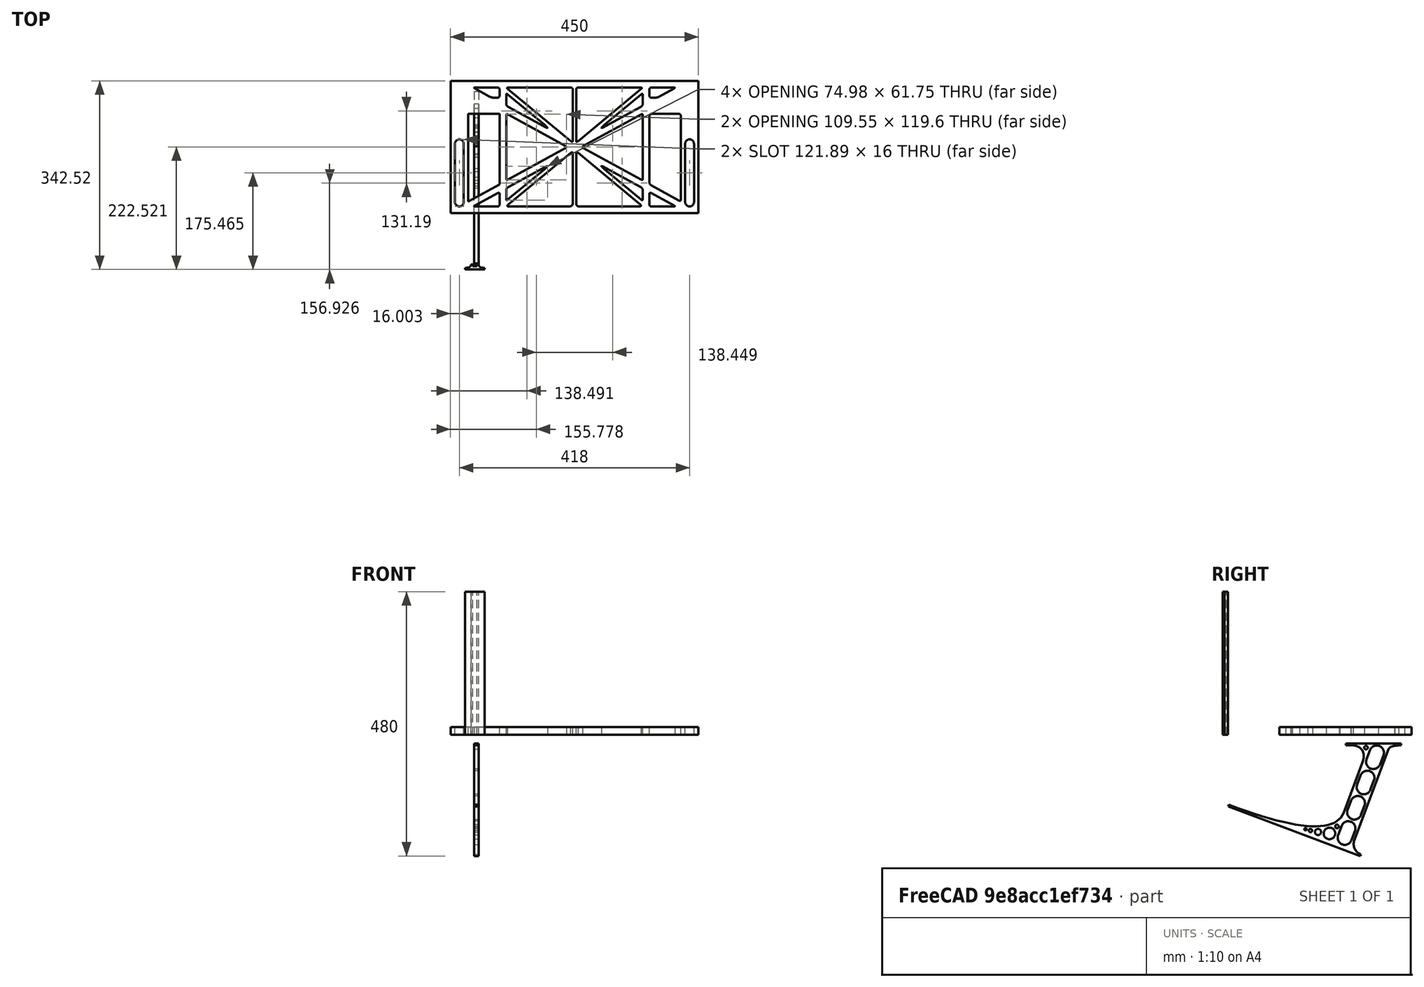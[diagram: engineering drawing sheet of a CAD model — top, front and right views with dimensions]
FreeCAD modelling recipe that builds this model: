
FCSTD DOCUMENT  (FreeCAD 0.19R0.19.2)
Label: laptopStand135FCStd
License: All rights reserved
LicenseURL: http://en.wikipedia.org/wiki/All_rights_reserved
objects: Sketcher::SketchObject×3, Part::Extrusion×3
note: 6 computed .brp shape members not serialized (recipe doc carries the construction recipe); baked Part::Feature solids carry a one-line shape summary decoded from their .brp

FEATURE [Sketcher::SketchObject] Sketch
  FullyConstrained = false
  sketch-geometry (352):
    g0: LineSegment StartX=-10.9272 StartY=-82.7794 StartZ=0 EndX=46.0728 EndY=-51.4823 EndZ=0
    g1: LineSegment StartX=-10.9272 StartY=76.4095 StartZ=0 EndX=-10.9272 EndY=-82.7794 EndZ=0
    g2: LineSegment StartX=46.0728 StartY=76.4095 StartZ=0 EndX=46.0728 EndY=-51.4823 EndZ=0
    g3: LineSegment StartX=-42.9272 StartY=136.221 StartZ=0 EndX=-42.9272 EndY=-103.779 EndZ=0
    g4: LineSegment StartX=407.073 StartY=136.221 StartZ=0 EndX=407.073 EndY=-103.779 EndZ=0
    g5: ArcOfCircle CenterX=-26.9272 CenterY=22.1087 CenterZ=0 NormalX=0 NormalY=0 NormalZ=1 AngleXU=0 Radius=8 StartAngle=4.1e-15 EndAngle=3.14159
    g6: ArcOfCircle CenterX=-26.9272 CenterY=-83.7794 CenterZ=0 NormalX=0 NormalY=0 NormalZ=1 AngleXU=0 Radius=8 StartAngle=3.14159 EndAngle=6.28319
    g7: LineSegment StartX=-34.9272 StartY=22.1087 StartZ=0 EndX=-34.9272 EndY=-83.7794 EndZ=0
    g8: LineSegment StartX=-18.9272 StartY=22.1087 StartZ=0 EndX=-18.9272 EndY=-83.7794 EndZ=0
    g9: ArcOfCircle CenterX=391.073 CenterY=22.1087 CenterZ=0 NormalX=0 NormalY=0 NormalZ=1 AngleXU=0 Radius=8 StartAngle=-4.4e-15 EndAngle=3.14159
    g10: LineSegment StartX=399.073 StartY=22.1087 StartZ=0 EndX=399.073 EndY=-83.7794 EndZ=0
    g11: LineSegment StartX=383.073 StartY=22.1087 StartZ=0 EndX=383.073 EndY=-83.7794 EndZ=0
    g12: ArcOfCircle CenterX=391.073 CenterY=-83.7794 CenterZ=0 NormalX=0 NormalY=0 NormalZ=1 AngleXU=0 Radius=8 StartAngle=3.14159 EndAngle=6.28319
    g13: Circle CenterX=175.022 CenterY=27.0628 CenterZ=0 NormalX=0 NormalY=0 NormalZ=1 AngleXU=0 Radius=1
    g14: Circle CenterX=179.022 CenterY=24.8665 CenterZ=0 NormalX=0 NormalY=0 NormalZ=1 AngleXU=0 Radius=1
    g15: Circle CenterX=179.022 CenterY=27.0628 CenterZ=0 NormalX=0 NormalY=0 NormalZ=1 AngleXU=0 Radius=1
    g16: BSplineCurve PolesCount=3 KnotsCount=2 Degree=2 IsPeriodic=0
    g17: GeomPoint X=175.022 Y=27.0628 Z=0
    g18: GeomPoint X=179.022 Y=27.0628 Z=0
    g19: Circle CenterX=189.124 CenterY=27.0628 CenterZ=0 NormalX=0 NormalY=0 NormalZ=1 AngleXU=0 Radius=1
    g20: Circle CenterX=185.124 CenterY=24.8665 CenterZ=0 NormalX=0 NormalY=0 NormalZ=1 AngleXU=0 Radius=1
    g21: Circle CenterX=185.124 CenterY=27.0628 CenterZ=0 NormalX=0 NormalY=0 NormalZ=1 AngleXU=0 Radius=1
    g22: BSplineCurve PolesCount=3 KnotsCount=2 Degree=2 IsPeriodic=0
    g23: GeomPoint X=189.124 Y=27.0628 Z=0
    g24: GeomPoint X=185.124 Y=27.0628 Z=0
    g25: Circle CenterX=175.022 CenterY=5.37834 CenterZ=0 NormalX=0 NormalY=0 NormalZ=1 AngleXU=0 Radius=1
    g26: Circle CenterX=179.022 CenterY=7.57463 CenterZ=0 NormalX=0 NormalY=0 NormalZ=1 AngleXU=0 Radius=1
    g27: Circle CenterX=179.022 CenterY=5.34704 CenterZ=0 NormalX=0 NormalY=0 NormalZ=1 AngleXU=0 Radius=1
    g28: BSplineCurve PolesCount=3 KnotsCount=2 Degree=2 IsPeriodic=0
    g29: GeomPoint X=175.022 Y=5.37834 Z=0
    g30: GeomPoint X=179.022 Y=5.34704 Z=0
    g31: Circle CenterX=189.124 CenterY=5.37834 CenterZ=0 NormalX=0 NormalY=0 NormalZ=1 AngleXU=0 Radius=1
    g32: Circle CenterX=185.124 CenterY=7.57463 CenterZ=0 NormalX=0 NormalY=0 NormalZ=1 AngleXU=0 Radius=1
    g33: Circle CenterX=185.124 CenterY=5.34704 CenterZ=0 NormalX=0 NormalY=0 NormalZ=1 AngleXU=0 Radius=1
    g34: BSplineCurve PolesCount=3 KnotsCount=2 Degree=2 IsPeriodic=0
    g35: GeomPoint X=189.124 Y=5.37834 Z=0
    g36: GeomPoint X=185.124 Y=5.34704 Z=0
    g37: Circle CenterX=165.871 CenterY=18.1458 CenterZ=0 NormalX=0 NormalY=0 NormalZ=1 AngleXU=0 Radius=1
    g38: Circle CenterX=169.377 CenterY=16.2206 CenterZ=0 NormalX=0 NormalY=0 NormalZ=1 AngleXU=0 Radius=1
    g39: Circle CenterX=165.871 CenterY=14.2954 CenterZ=0 NormalX=0 NormalY=0 NormalZ=1 AngleXU=0 Radius=1
    g40: BSplineCurve PolesCount=3 KnotsCount=2 Degree=2 IsPeriodic=0
    g41: GeomPoint X=165.871 Y=18.1458 Z=0
    g42: GeomPoint X=165.871 Y=14.2954 Z=0
    g43: Circle CenterX=198.275 CenterY=18.1458 CenterZ=0 NormalX=0 NormalY=0 NormalZ=1 AngleXU=0 Radius=1
    g44: Circle CenterX=194.768 CenterY=16.2206 CenterZ=0 NormalX=0 NormalY=0 NormalZ=1 AngleXU=0 Radius=1
    g45: Circle CenterX=198.275 CenterY=14.2954 CenterZ=0 NormalX=0 NormalY=0 NormalZ=1 AngleXU=0 Radius=1
    g46: BSplineCurve PolesCount=3 KnotsCount=2 Degree=2 IsPeriodic=0
    g47: GeomPoint X=198.275 Y=18.1458 Z=0
    g48: GeomPoint X=198.275 Y=14.2954 Z=0
    g49: LineSegment StartX=407.073 StartY=-103.779 StartZ=0 EndX=-42.9272 EndY=-103.779 EndZ=0
    g50: LineSegment StartX=407.073 StartY=136.221 StartZ=0 EndX=-42.9272 EndY=136.221 EndZ=0
    g51: LineSegment StartX=46.0728 StartY=76.4095 StartZ=0 EndX=-10.9272 EndY=76.4095 EndZ=0
    g52: Circle CenterX=125.607 CenterY=54.1951 CenterZ=0 NormalX=0 NormalY=0 NormalZ=1 AngleXU=0 Radius=1
    g53: Circle CenterX=139.632 CenterY=46.4944 CenterZ=0 NormalX=0 NormalY=0 NormalZ=1 AngleXU=0 Radius=1
    g54: Circle CenterX=127.326 CenterY=56.7187 CenterZ=0 NormalX=0 NormalY=0 NormalZ=1 AngleXU=0 Radius=1
    g55: BSplineCurve PolesCount=3 KnotsCount=2 Degree=2 IsPeriodic=0
    g56: GeomPoint X=125.607 Y=54.1951 Z=0
    g57: GeomPoint X=127.326 Y=56.7187 Z=0
    g58: Circle CenterX=236.821 CenterY=56.7187 CenterZ=0 NormalX=0 NormalY=0 NormalZ=1 AngleXU=0 Radius=1
    g59: Circle CenterX=224.513 CenterY=46.4944 CenterZ=0 NormalX=0 NormalY=0 NormalZ=1 AngleXU=0 Radius=1
    g60: Circle CenterX=238.538 CenterY=54.1951 CenterZ=0 NormalX=0 NormalY=0 NormalZ=1 AngleXU=0 Radius=1
    g61: BSplineCurve PolesCount=3 KnotsCount=2 Degree=2 IsPeriodic=0
    g62: GeomPoint X=236.821 Y=56.7187 Z=0
    g63: GeomPoint X=238.538 Y=54.1951 Z=0
    g64: Circle CenterX=238.538 CenterY=-21.7539 CenterZ=0 NormalX=0 NormalY=0 NormalZ=1 AngleXU=0 Radius=1
    g65: Circle CenterX=224.513 CenterY=-14.0532 CenterZ=0 NormalX=0 NormalY=0 NormalZ=1 AngleXU=0 Radius=1
    g66: Circle CenterX=236.821 CenterY=-24.2775 CenterZ=0 NormalX=0 NormalY=0 NormalZ=1 AngleXU=0 Radius=1
    g67: BSplineCurve PolesCount=3 KnotsCount=2 Degree=2 IsPeriodic=0
    g68: GeomPoint X=238.538 Y=-21.7539 Z=0
    g69: GeomPoint X=236.821 Y=-24.2775 Z=0
    g70: Circle CenterX=125.607 CenterY=-21.7539 CenterZ=0 NormalX=0 NormalY=0 NormalZ=1 AngleXU=0 Radius=1
    g71: Circle CenterX=139.632 CenterY=-14.0532 CenterZ=0 NormalX=0 NormalY=0 NormalZ=1 AngleXU=0 Radius=1
    g72: Circle CenterX=127.325 CenterY=-24.2775 CenterZ=0 NormalX=0 NormalY=0 NormalZ=1 AngleXU=0 Radius=1
    g73: BSplineCurve PolesCount=3 KnotsCount=2 Degree=2 IsPeriodic=0
    g74: GeomPoint X=125.607 Y=-21.7539 Z=0
    g75: GeomPoint X=127.325 Y=-24.2775 Z=0
    g76: Circle CenterX=302.996 CenterY=111.695 CenterZ=0 NormalX=0 NormalY=0 NormalZ=1 AngleXU=0 Radius=1
    g77: Circle CenterX=306.073 CenterY=114.251 CenterZ=0 NormalX=0 NormalY=0 NormalZ=1 AngleXU=0 Radius=1
    g78: Circle CenterX=306.073 CenterY=110.251 CenterZ=0 NormalX=0 NormalY=0 NormalZ=1 AngleXU=0 Radius=1
    g79: BSplineCurve PolesCount=3 KnotsCount=2 Degree=2 IsPeriodic=0
    g80: GeomPoint X=302.996 Y=111.695 Z=0
    g81: GeomPoint X=306.073 Y=110.251 Z=0
    g82: Circle CenterX=306.073 CenterY=95.2763 CenterZ=0 NormalX=0 NormalY=0 NormalZ=1 AngleXU=0 Radius=1
    g83: Circle CenterX=306.073 CenterY=91.2763 CenterZ=0 NormalX=0 NormalY=0 NormalZ=1 AngleXU=0 Radius=1
    g84: Circle CenterX=302.567 CenterY=89.3511 CenterZ=0 NormalX=0 NormalY=0 NormalZ=1 AngleXU=0 Radius=1
    g85: BSplineCurve PolesCount=3 KnotsCount=2 Degree=2 IsPeriodic=0
    g86: GeomPoint X=306.073 Y=95.2763 Z=0
    g87: GeomPoint X=302.567 Y=89.3511 Z=0
    g88: LineSegment StartX=306.073 StartY=110.251 StartZ=0 EndX=306.073 EndY=95.2763 EndZ=0
    g89: LineSegment StartX=302.996 StartY=111.695 StartZ=0 EndX=236.821 EndY=56.7187 EndZ=0
    g90: LineSegment StartX=238.538 StartY=54.1951 StartZ=0 EndX=302.567 EndY=89.3511 EndZ=0
    g91: Circle CenterX=61.1496 CenterY=111.695 CenterZ=0 NormalX=0 NormalY=0 NormalZ=1 AngleXU=0 Radius=1
    g92: Circle CenterX=58.0728 CenterY=114.251 CenterZ=0 NormalX=0 NormalY=0 NormalZ=1 AngleXU=0 Radius=1
    g93: Circle CenterX=58.0728 CenterY=110.251 CenterZ=0 NormalX=0 NormalY=0 NormalZ=1 AngleXU=0 Radius=1
    g94: BSplineCurve PolesCount=3 KnotsCount=2 Degree=2 IsPeriodic=0
    g95: GeomPoint X=61.1496 Y=111.695 Z=0
    g96: GeomPoint X=58.0728 Y=110.251 Z=0
    g97: Circle CenterX=61.5791 CenterY=89.3511 CenterZ=0 NormalX=0 NormalY=0 NormalZ=1 AngleXU=0 Radius=1
    g98: Circle CenterX=58.0728 CenterY=91.2763 CenterZ=0 NormalX=0 NormalY=0 NormalZ=1 AngleXU=0 Radius=1
    g99: Circle CenterX=58.0728 CenterY=95.2763 CenterZ=0 NormalX=0 NormalY=0 NormalZ=1 AngleXU=0 Radius=1
    g100: BSplineCurve PolesCount=3 KnotsCount=2 Degree=2 IsPeriodic=0
    g101: GeomPoint X=61.5791 Y=89.3511 Z=0
    g102: GeomPoint X=58.0728 Y=95.2763 Z=0
    g103: LineSegment StartX=58.0728 StartY=110.251 StartZ=0 EndX=58.0728 EndY=95.2763 EndZ=0
    g104: LineSegment StartX=61.1496 StartY=111.695 StartZ=0 EndX=127.326 EndY=56.7187 EndZ=0
    g105: LineSegment StartX=125.607 StartY=54.1951 StartZ=0 EndX=61.5791 EndY=89.3511 EndZ=0
    g106: Circle CenterX=61.5791 CenterY=-56.9099 CenterZ=0 NormalX=0 NormalY=0 NormalZ=1 AngleXU=0 Radius=1
    g107: Circle CenterX=58.0728 CenterY=-58.8351 CenterZ=0 NormalX=0 NormalY=0 NormalZ=1 AngleXU=0 Radius=1
    g108: Circle CenterX=58.0728 CenterY=-62.8351 CenterZ=0 NormalX=0 NormalY=0 NormalZ=1 AngleXU=0 Radius=1
    g109: BSplineCurve PolesCount=3 KnotsCount=2 Degree=2 IsPeriodic=0
    g110: GeomPoint X=61.5791 Y=-56.9099 Z=0
    g111: GeomPoint X=58.0728 Y=-62.8351 Z=0
    g112: Circle CenterX=58.0728 CenterY=-77.8102 CenterZ=0 NormalX=0 NormalY=0 NormalZ=1 AngleXU=0 Radius=1
    g113: Circle CenterX=58.0728 CenterY=-81.8102 CenterZ=0 NormalX=0 NormalY=0 NormalZ=1 AngleXU=0 Radius=1
    g114: Circle CenterX=61.1496 CenterY=-79.2541 CenterZ=0 NormalX=0 NormalY=0 NormalZ=1 AngleXU=0 Radius=1
    g115: BSplineCurve PolesCount=3 KnotsCount=2 Degree=2 IsPeriodic=0
    g116: GeomPoint X=58.0728 Y=-77.8102 Z=0
    g117: GeomPoint X=61.1496 Y=-79.2541 Z=0
    g118: LineSegment StartX=58.0728 StartY=-62.8351 StartZ=0 EndX=58.0728 EndY=-77.8102 EndZ=0
    g119: LineSegment StartX=61.1496 StartY=-79.2541 StartZ=0 EndX=127.325 EndY=-24.2775 EndZ=0
    g120: LineSegment StartX=125.607 StartY=-21.7539 StartZ=0 EndX=61.5791 EndY=-56.9099 EndZ=0
    g121: Circle CenterX=302.567 CenterY=-56.9099 CenterZ=0 NormalX=0 NormalY=0 NormalZ=1 AngleXU=0 Radius=1
    g122: Circle CenterX=306.073 CenterY=-58.8351 CenterZ=0 NormalX=0 NormalY=0 NormalZ=1 AngleXU=0 Radius=1
    g123: Circle CenterX=306.073 CenterY=-62.8351 CenterZ=0 NormalX=0 NormalY=0 NormalZ=1 AngleXU=0 Radius=1
    g124: BSplineCurve PolesCount=3 KnotsCount=2 Degree=2 IsPeriodic=0
    g125: GeomPoint X=302.567 Y=-56.9099 Z=0
    g126: GeomPoint X=306.073 Y=-62.8351 Z=0
    g127: Circle CenterX=302.996 CenterY=-79.2541 CenterZ=0 NormalX=0 NormalY=0 NormalZ=1 AngleXU=0 Radius=1
    g128: Circle CenterX=306.073 CenterY=-81.8102 CenterZ=0 NormalX=0 NormalY=0 NormalZ=1 AngleXU=0 Radius=1
    g129: Circle CenterX=306.073 CenterY=-77.8102 CenterZ=0 NormalX=0 NormalY=0 NormalZ=1 AngleXU=0 Radius=1
    g130: BSplineCurve PolesCount=3 KnotsCount=2 Degree=2 IsPeriodic=0
    g131: GeomPoint X=302.996 Y=-79.2541 Z=0
    g132: GeomPoint X=306.073 Y=-77.8102 Z=0
    g133: LineSegment StartX=306.073 StartY=-62.8351 StartZ=0 EndX=306.073 EndY=-77.8102 EndZ=0
    g134: LineSegment StartX=302.996 StartY=-79.2541 StartZ=0 EndX=236.821 EndY=-24.2775 EndZ=0
    g135: LineSegment StartX=238.538 StartY=-21.7539 StartZ=0 EndX=302.567 EndY=-56.9099 EndZ=0
    g136: Circle CenterX=61.6457 CenterY=-88.8112 CenterZ=0 NormalX=0 NormalY=0 NormalZ=1 AngleXU=0 Radius=1
    g137: Circle CenterX=58.0728 CenterY=-91.7794 CenterZ=0 NormalX=0 NormalY=0 NormalZ=1 AngleXU=0 Radius=1
    g138: Circle CenterX=63.9135 CenterY=-91.7794 CenterZ=0 NormalX=0 NormalY=0 NormalZ=1 AngleXU=0 Radius=1
    g139: BSplineCurve PolesCount=3 KnotsCount=2 Degree=2 IsPeriodic=0
    g140: GeomPoint X=61.6457 Y=-88.8112 Z=0
    g141: GeomPoint X=63.9135 Y=-91.7794 Z=0
    g142: Circle CenterX=179.022 CenterY=-85.8163 CenterZ=0 NormalX=0 NormalY=0 NormalZ=1 AngleXU=0 Radius=1
    g143: Circle CenterX=179.022 CenterY=-91.7794 CenterZ=0 NormalX=0 NormalY=0 NormalZ=1 AngleXU=0 Radius=1
    g144: Circle CenterX=171.895 CenterY=-91.7794 CenterZ=0 NormalX=0 NormalY=0 NormalZ=1 AngleXU=0 Radius=1
    g145: BSplineCurve PolesCount=3 KnotsCount=2 Degree=2 IsPeriodic=0
    g146: GeomPoint X=179.022 Y=-85.8163 Z=0
    g147: GeomPoint X=171.895 Y=-91.7794 Z=0
    g148: Circle CenterX=185.124 CenterY=-86.2028 CenterZ=0 NormalX=0 NormalY=0 NormalZ=1 AngleXU=0 Radius=1
    g149: Circle CenterX=185.124 CenterY=-91.7794 CenterZ=0 NormalX=0 NormalY=0 NormalZ=1 AngleXU=0 Radius=1
    g150: Circle CenterX=191.747 CenterY=-91.7794 CenterZ=0 NormalX=0 NormalY=0 NormalZ=1 AngleXU=0 Radius=1
    g151: BSplineCurve PolesCount=3 KnotsCount=2 Degree=2 IsPeriodic=0
    g152: GeomPoint X=185.124 Y=-86.2028 Z=0
    g153: GeomPoint X=191.747 Y=-91.7794 Z=0
    g154: Circle CenterX=299.888 CenterY=-86.6413 CenterZ=0 NormalX=0 NormalY=0 NormalZ=1 AngleXU=0 Radius=1
    g155: Circle CenterX=306.073 CenterY=-91.7794 CenterZ=0 NormalX=0 NormalY=0 NormalZ=1 AngleXU=0 Radius=1
    g156: Circle CenterX=298.776 CenterY=-91.7794 CenterZ=0 NormalX=0 NormalY=0 NormalZ=1 AngleXU=0 Radius=1
    g157: BSplineCurve PolesCount=3 KnotsCount=2 Degree=2 IsPeriodic=0
    g158: GeomPoint X=299.888 Y=-86.6413 Z=0
    g159: GeomPoint X=298.776 Y=-91.7794 Z=0
    g160: LineSegment StartX=189.124 StartY=5.37834 StartZ=0 EndX=299.888 EndY=-86.6413 EndZ=0
    g161: LineSegment StartX=298.776 StartY=-91.7794 StartZ=0 EndX=191.747 EndY=-91.7794 EndZ=0
    g162: LineSegment StartX=185.124 StartY=-86.2028 StartZ=0 EndX=185.124 EndY=5.34704 EndZ=0
    g163: LineSegment StartX=179.022 StartY=5.34704 StartZ=0 EndX=179.022 EndY=-85.8163 EndZ=0
    g164: LineSegment StartX=171.895 StartY=-91.7794 StartZ=0 EndX=63.9135 EndY=-91.7794 EndZ=0
    g165: LineSegment StartX=61.6457 StartY=-88.8112 StartZ=0 EndX=175.022 EndY=5.37834 EndZ=0
    g166: Circle CenterX=302.073 CenterY=124.221 CenterZ=0 NormalX=0 NormalY=0 NormalZ=1 AngleXU=0 Radius=1
    g167: Circle CenterX=306.073 CenterY=124.221 CenterZ=0 NormalX=0 NormalY=0 NormalZ=1 AngleXU=0 Radius=1
    g168: Circle CenterX=302.996 CenterY=121.665 CenterZ=0 NormalX=0 NormalY=0 NormalZ=1 AngleXU=0 Radius=1
    g169: BSplineCurve PolesCount=3 KnotsCount=2 Degree=2 IsPeriodic=0
    g170: GeomPoint X=302.073 Y=124.221 Z=0
    g171: GeomPoint X=302.996 Y=121.665 Z=0
    g172: Circle CenterX=189.124 CenterY=124.221 CenterZ=0 NormalX=0 NormalY=0 NormalZ=1 AngleXU=0 Radius=1
    g173: Circle CenterX=185.124 CenterY=124.221 CenterZ=0 NormalX=0 NormalY=0 NormalZ=1 AngleXU=0 Radius=1
    g174: Circle CenterX=185.124 CenterY=120.221 CenterZ=0 NormalX=0 NormalY=0 NormalZ=1 AngleXU=0 Radius=1
    g175: BSplineCurve PolesCount=3 KnotsCount=2 Degree=2 IsPeriodic=0
    g176: GeomPoint X=189.124 Y=124.221 Z=0
    g177: GeomPoint X=185.124 Y=120.221 Z=0
    g178: Circle CenterX=175.022 CenterY=124.221 CenterZ=0 NormalX=0 NormalY=0 NormalZ=1 AngleXU=0 Radius=1
    g179: Circle CenterX=179.022 CenterY=124.221 CenterZ=0 NormalX=0 NormalY=0 NormalZ=1 AngleXU=0 Radius=1
    g180: Circle CenterX=179.022 CenterY=120.221 CenterZ=0 NormalX=0 NormalY=0 NormalZ=1 AngleXU=0 Radius=1
    g181: BSplineCurve PolesCount=3 KnotsCount=2 Degree=2 IsPeriodic=0
    g182: GeomPoint X=175.022 Y=124.221 Z=0
    g183: GeomPoint X=179.022 Y=120.221 Z=0
    g184: Circle CenterX=62.0728 CenterY=124.221 CenterZ=0 NormalX=0 NormalY=0 NormalZ=1 AngleXU=0 Radius=1
    g185: Circle CenterX=58.0728 CenterY=124.221 CenterZ=0 NormalX=0 NormalY=0 NormalZ=1 AngleXU=0 Radius=1
    g186: Circle CenterX=61.1496 CenterY=121.665 CenterZ=0 NormalX=0 NormalY=0 NormalZ=1 AngleXU=0 Radius=1
    g187: BSplineCurve PolesCount=3 KnotsCount=2 Degree=2 IsPeriodic=0
    g188: GeomPoint X=62.0728 Y=124.221 Z=0
    g189: GeomPoint X=61.1496 Y=121.665 Z=0
    g190: LineSegment StartX=62.0728 StartY=124.221 StartZ=0 EndX=175.022 EndY=124.221 EndZ=0
    g191: LineSegment StartX=179.022 StartY=120.221 StartZ=0 EndX=179.022 EndY=27.0628 EndZ=0
    g192: LineSegment StartX=185.124 StartY=27.0628 StartZ=0 EndX=185.124 EndY=120.221 EndZ=0
    g193: LineSegment StartX=189.124 StartY=124.221 StartZ=0 EndX=302.073 EndY=124.221 EndZ=0
    g194: LineSegment StartX=302.996 StartY=121.665 StartZ=0 EndX=189.124 EndY=27.0628 EndZ=0
    g195: LineSegment StartX=175.022 StartY=27.0628 StartZ=0 EndX=61.1496 EndY=121.665 EndZ=0
    g196: Circle CenterX=61.5791 CenterY=75.4095 CenterZ=0 NormalX=0 NormalY=0 NormalZ=1 AngleXU=0 Radius=1
    g197: Circle CenterX=58.0728 CenterY=77.3346 CenterZ=0 NormalX=0 NormalY=0 NormalZ=1 AngleXU=0 Radius=1
    g198: Circle CenterX=58.0728 CenterY=73.3346 CenterZ=0 NormalX=0 NormalY=0 NormalZ=1 AngleXU=0 Radius=1
    g199: BSplineCurve PolesCount=3 KnotsCount=2 Degree=2 IsPeriodic=0
    g200: GeomPoint X=61.5791 Y=75.4095 Z=0
    g201: GeomPoint X=58.0728 Y=73.3346 Z=0
    g202: Circle CenterX=58.0728 CenterY=-40.8935 CenterZ=0 NormalX=0 NormalY=0 NormalZ=1 AngleXU=0 Radius=1
    g203: Circle CenterX=58.0728 CenterY=-44.8935 CenterZ=0 NormalX=0 NormalY=0 NormalZ=1 AngleXU=0 Radius=1
    g204: Circle CenterX=61.5791 CenterY=-42.9683 CenterZ=0 NormalX=0 NormalY=0 NormalZ=1 AngleXU=0 Radius=1
    g205: BSplineCurve PolesCount=3 KnotsCount=2 Degree=2 IsPeriodic=0
    g206: GeomPoint X=58.0728 Y=-40.8935 Z=0
    g207: GeomPoint X=61.5791 Y=-42.9683 Z=0
    g208: LineSegment StartX=61.5791 StartY=-42.9683 StartZ=0 EndX=165.871 EndY=14.2954 EndZ=0
    g209: LineSegment StartX=165.871 StartY=18.1458 StartZ=0 EndX=61.5791 EndY=75.4095 EndZ=0
    g210: LineSegment StartX=58.0728 StartY=73.3346 StartZ=0 EndX=58.0728 EndY=-40.8935 EndZ=0
    g211: Circle CenterX=302.567 CenterY=-42.9683 CenterZ=0 NormalX=0 NormalY=0 NormalZ=1 AngleXU=0 Radius=1
    g212: Circle CenterX=306.073 CenterY=-44.8935 CenterZ=0 NormalX=0 NormalY=0 NormalZ=1 AngleXU=0 Radius=1
    g213: Circle CenterX=306.073 CenterY=-40.8935 CenterZ=0 NormalX=0 NormalY=0 NormalZ=1 AngleXU=0 Radius=1
    g214: BSplineCurve PolesCount=3 KnotsCount=2 Degree=2 IsPeriodic=0
    g215: GeomPoint X=302.567 Y=-42.9683 Z=0
    g216: GeomPoint X=306.073 Y=-40.8935 Z=0
    g217: Circle CenterX=306.073 CenterY=73.3346 CenterZ=0 NormalX=0 NormalY=0 NormalZ=1 AngleXU=0 Radius=1
    g218: Circle CenterX=306.073 CenterY=77.3346 CenterZ=0 NormalX=0 NormalY=0 NormalZ=1 AngleXU=0 Radius=1
    g219: Circle CenterX=302.567 CenterY=75.4095 CenterZ=0 NormalX=0 NormalY=0 NormalZ=1 AngleXU=0 Radius=1
    g220: BSplineCurve PolesCount=3 KnotsCount=2 Degree=2 IsPeriodic=0
    g221: GeomPoint X=306.073 Y=73.3346 Z=0
    g222: GeomPoint X=302.567 Y=75.4095 Z=0
    g223: LineSegment StartX=302.567 StartY=-42.9683 StartZ=0 EndX=198.275 EndY=14.2954 EndZ=0
    g224: LineSegment StartX=198.275 StartY=18.1458 StartZ=0 EndX=302.567 EndY=75.4095 EndZ=0
    g225: LineSegment StartX=306.073 StartY=73.3346 StartZ=0 EndX=306.073 EndY=-40.8935 EndZ=0
    g226: LineSegment StartX=322.073 StartY=105.865 StartZ=0 EndX=328.643 EndY=105.865 EndZ=0
    g227: LineSegment StartX=318.073 StartY=120.221 StartZ=0 EndX=318.073 EndY=109.865 EndZ=0
    g228: LineSegment StartX=336.157 StartY=107.779 StartZ=0 EndX=362.567 EndY=122.294 EndZ=0
    g229: Circle CenterX=362.073 CenterY=124.221 CenterZ=0 NormalX=0 NormalY=0 NormalZ=1 AngleXU=0 Radius=1
    g230: Circle CenterX=366.073 CenterY=124.221 CenterZ=0 NormalX=0 NormalY=0 NormalZ=1 AngleXU=0 Radius=1
    g231: Circle CenterX=362.567 CenterY=122.294 CenterZ=0 NormalX=0 NormalY=0 NormalZ=1 AngleXU=0 Radius=1
    g232: BSplineCurve PolesCount=3 KnotsCount=2 Degree=2 IsPeriodic=0
    g233: GeomPoint X=362.073 Y=124.221 Z=0
    g234: GeomPoint X=362.567 Y=122.294 Z=0
    g235: Circle CenterX=322.073 CenterY=124.221 CenterZ=0 NormalX=0 NormalY=0 NormalZ=1 AngleXU=0 Radius=1
    g236: Circle CenterX=318.073 CenterY=124.221 CenterZ=0 NormalX=0 NormalY=0 NormalZ=1 AngleXU=0 Radius=1
    g237: Circle CenterX=318.073 CenterY=120.221 CenterZ=0 NormalX=0 NormalY=0 NormalZ=1 AngleXU=0 Radius=1
    g238: BSplineCurve PolesCount=3 KnotsCount=2 Degree=2 IsPeriodic=0
    g239: GeomPoint X=322.073 Y=124.221 Z=0
    g240: GeomPoint X=318.073 Y=120.221 Z=0
    g241: Circle CenterX=322.073 CenterY=105.865 CenterZ=0 NormalX=0 NormalY=0 NormalZ=1 AngleXU=0 Radius=1
    g242: Circle CenterX=318.073 CenterY=105.865 CenterZ=0 NormalX=0 NormalY=0 NormalZ=1 AngleXU=0 Radius=1
    g243: Circle CenterX=318.073 CenterY=109.865 CenterZ=0 NormalX=0 NormalY=0 NormalZ=1 AngleXU=0 Radius=1
    g244: BSplineCurve PolesCount=3 KnotsCount=2 Degree=2 IsPeriodic=0
    g245: GeomPoint X=322.073 Y=105.865 Z=0
    g246: GeomPoint X=318.073 Y=109.865 Z=0
    g247: Circle CenterX=336.157 CenterY=107.779 CenterZ=0 NormalX=0 NormalY=0 NormalZ=1 AngleXU=0 Radius=1
    g248: Circle CenterX=332.651 CenterY=105.853 CenterZ=0 NormalX=0 NormalY=0 NormalZ=1 AngleXU=0 Radius=1
    g249: Circle CenterX=328.643 CenterY=105.865 CenterZ=0 NormalX=0 NormalY=0 NormalZ=1 AngleXU=0 Radius=1
    g250: BSplineCurve PolesCount=3 KnotsCount=2 Degree=2 IsPeriodic=0
    g251: GeomPoint X=336.157 Y=107.779 Z=0
    g252: GeomPoint X=328.643 Y=105.865 Z=0
    g253: LineSegment StartX=322.073 StartY=124.221 StartZ=0 EndX=362.073 EndY=124.221 EndZ=0
    g254: Circle CenterX=371.567 CenterY=-80.8644 CenterZ=0 NormalX=0 NormalY=0 NormalZ=1 AngleXU=0 Radius=1
    g255: Circle CenterX=375.073 CenterY=-82.7896 CenterZ=0 NormalX=0 NormalY=0 NormalZ=1 AngleXU=0 Radius=1
    g256: Circle CenterX=375.073 CenterY=-78.7896 CenterZ=0 NormalX=0 NormalY=0 NormalZ=1 AngleXU=0 Radius=1
    g257: BSplineCurve PolesCount=3 KnotsCount=2 Degree=2 IsPeriodic=0
    g258: GeomPoint X=371.567 Y=-80.8644 Z=0
    g259: GeomPoint X=375.073 Y=-78.7896 Z=0
    g260: Circle CenterX=321.579 CenterY=-53.4075 CenterZ=0 NormalX=0 NormalY=0 NormalZ=1 AngleXU=0 Radius=1
    g261: Circle CenterX=318.073 CenterY=-51.4823 CenterZ=0 NormalX=0 NormalY=0 NormalZ=1 AngleXU=0 Radius=1
    g262: Circle CenterX=318.073 CenterY=-47.4823 CenterZ=0 NormalX=0 NormalY=0 NormalZ=1 AngleXU=0 Radius=1
    g263: BSplineCurve PolesCount=3 KnotsCount=2 Degree=2 IsPeriodic=0
    g264: GeomPoint X=321.579 Y=-53.4075 Z=0
    g265: GeomPoint X=318.073 Y=-47.4823 Z=0
    g266: LineSegment StartX=371.567 StartY=-80.8644 StartZ=0 EndX=321.579 EndY=-53.4075 EndZ=0
    g267: Circle CenterX=321.579 CenterY=-67.3492 CenterZ=0 NormalX=0 NormalY=0 NormalZ=1 AngleXU=0 Radius=1
    g268: Circle CenterX=318.073 CenterY=-65.424 CenterZ=0 NormalX=0 NormalY=0 NormalZ=1 AngleXU=0 Radius=1
    g269: Circle CenterX=318.073 CenterY=-69.424 CenterZ=0 NormalX=0 NormalY=0 NormalZ=1 AngleXU=0 Radius=1
    g270: BSplineCurve PolesCount=3 KnotsCount=2 Degree=2 IsPeriodic=0
    g271: GeomPoint X=321.579 Y=-67.3492 Z=0
    g272: GeomPoint X=318.073 Y=-69.424 Z=0
    g273: Circle CenterX=362.567 CenterY=-89.8542 CenterZ=0 NormalX=0 NormalY=0 NormalZ=1 AngleXU=0 Radius=1
    g274: Circle CenterX=366.073 CenterY=-91.7794 CenterZ=0 NormalX=0 NormalY=0 NormalZ=1 AngleXU=0 Radius=1
    g275: Circle CenterX=362.073 CenterY=-91.7794 CenterZ=0 NormalX=0 NormalY=0 NormalZ=1 AngleXU=0 Radius=1
    g276: BSplineCurve PolesCount=3 KnotsCount=2 Degree=2 IsPeriodic=0
    g277: GeomPoint X=362.567 Y=-89.8542 Z=0
    g278: GeomPoint X=362.073 Y=-91.7794 Z=0
    g279: Circle CenterX=322.073 CenterY=-91.7794 CenterZ=0 NormalX=0 NormalY=0 NormalZ=1 AngleXU=0 Radius=1
    g280: Circle CenterX=318.073 CenterY=-91.7794 CenterZ=0 NormalX=0 NormalY=0 NormalZ=1 AngleXU=0 Radius=1
    g281: Circle CenterX=318.073 CenterY=-87.7794 CenterZ=0 NormalX=0 NormalY=0 NormalZ=1 AngleXU=0 Radius=1
    g282: BSplineCurve PolesCount=3 KnotsCount=2 Degree=2 IsPeriodic=0
    g283: GeomPoint X=322.073 Y=-91.7794 Z=0
    g284: GeomPoint X=318.073 Y=-87.7794 Z=0
    g285: LineSegment StartX=362.567 StartY=-89.8542 StartZ=0 EndX=321.579 EndY=-67.3492 EndZ=0
    g286: LineSegment StartX=318.073 StartY=-69.424 StartZ=0 EndX=318.073 EndY=-87.7794 EndZ=0
    g287: LineSegment StartX=322.073 StartY=-91.7794 StartZ=0 EndX=362.073 EndY=-91.7794 EndZ=0
    g288: Circle CenterX=2.07281 CenterY=124.221 CenterZ=0 NormalX=0 NormalY=0 NormalZ=1 AngleXU=0 Radius=1
    g289: Circle CenterX=1.57905 CenterY=122.295 CenterZ=0 NormalX=0 NormalY=0 NormalZ=1 AngleXU=0 Radius=1
    g290: BSplineCurve PolesCount=3 KnotsCount=2 Degree=2 IsPeriodic=0
    g291: GeomPoint X=2.07281 Y=124.221 Z=0
    g292: GeomPoint X=1.57905 Y=122.295 Z=0
    g293: Circle CenterX=42.0728 CenterY=124.221 CenterZ=0 NormalX=0 NormalY=0 NormalZ=1 AngleXU=0 Radius=1
    g294: Circle CenterX=46.0728 CenterY=124.221 CenterZ=0 NormalX=0 NormalY=0 NormalZ=1 AngleXU=0 Radius=1
    g295: Circle CenterX=46.0728 CenterY=120.221 CenterZ=0 NormalX=0 NormalY=0 NormalZ=1 AngleXU=0 Radius=1
    g296: BSplineCurve PolesCount=3 KnotsCount=2 Degree=2 IsPeriodic=0
    g297: GeomPoint X=42.0728 Y=124.221 Z=0
    g298: GeomPoint X=46.0728 Y=120.221 Z=0
    g299: Circle CenterX=46.0728 CenterY=109.865 CenterZ=0 NormalX=0 NormalY=0 NormalZ=1 AngleXU=0 Radius=1
    g300: Circle CenterX=46.0728 CenterY=105.865 CenterZ=0 NormalX=0 NormalY=0 NormalZ=1 AngleXU=0 Radius=1
    g301: Circle CenterX=42.0728 CenterY=105.865 CenterZ=0 NormalX=0 NormalY=0 NormalZ=1 AngleXU=0 Radius=1
    g302: BSplineCurve PolesCount=3 KnotsCount=2 Degree=2 IsPeriodic=0
    g303: GeomPoint X=46.0728 Y=109.865 Z=0
    g304: GeomPoint X=42.0728 Y=105.865 Z=0
    g305: Circle CenterX=35.5028 CenterY=105.865 CenterZ=0 NormalX=0 NormalY=0 NormalZ=1 AngleXU=0 Radius=1
    g306: Circle CenterX=31.5028 CenterY=105.865 CenterZ=0 NormalX=0 NormalY=0 NormalZ=1 AngleXU=0 Radius=1
    g307: Circle CenterX=27.9965 CenterY=107.79 CenterZ=0 NormalX=0 NormalY=0 NormalZ=1 AngleXU=0 Radius=1
    g308: BSplineCurve PolesCount=3 KnotsCount=2 Degree=2 IsPeriodic=0
    g309: GeomPoint X=35.5028 Y=105.865 Z=0
    g310: GeomPoint X=27.9965 Y=107.79 Z=0
    g311: LineSegment StartX=2.07281 StartY=124.221 StartZ=0 EndX=42.0728 EndY=124.221 EndZ=0
    g312: LineSegment StartX=46.0728 StartY=120.221 StartZ=0 EndX=46.0728 EndY=109.865 EndZ=0
    g313: LineSegment StartX=42.0728 StartY=105.865 StartZ=0 EndX=35.5028 EndY=105.865 EndZ=0
    g314: LineSegment StartX=27.9965 StartY=107.79 StartZ=0 EndX=1.57905 EndY=122.295 EndZ=0
    g315: Circle CenterX=42.5666 CenterY=-67.3492 CenterZ=0 NormalX=0 NormalY=0 NormalZ=1 AngleXU=0 Radius=1
    g316: Circle CenterX=46.0728 CenterY=-65.424 CenterZ=0 NormalX=0 NormalY=0 NormalZ=1 AngleXU=0 Radius=1
    g317: Circle CenterX=46.0728 CenterY=-69.424 CenterZ=0 NormalX=0 NormalY=0 NormalZ=1 AngleXU=0 Radius=1
    g318: BSplineCurve PolesCount=3 KnotsCount=2 Degree=2 IsPeriodic=0
    g319: GeomPoint X=42.5666 Y=-67.3492 Z=0
    g320: GeomPoint X=46.0728 Y=-69.424 Z=0
    g321: Circle CenterX=46.0728 CenterY=-87.7794 CenterZ=0 NormalX=0 NormalY=0 NormalZ=1 AngleXU=0 Radius=1
    g322: Circle CenterX=46.0728 CenterY=-91.7794 CenterZ=0 NormalX=0 NormalY=0 NormalZ=1 AngleXU=0 Radius=1
    g323: Circle CenterX=42.0728 CenterY=-91.7794 CenterZ=0 NormalX=0 NormalY=0 NormalZ=1 AngleXU=0 Radius=1
    g324: BSplineCurve PolesCount=3 KnotsCount=2 Degree=2 IsPeriodic=0
    g325: GeomPoint X=46.0728 Y=-87.7794 Z=0
    g326: GeomPoint X=42.0728 Y=-91.7794 Z=0
    g327: Circle CenterX=2.07281 CenterY=-91.7794 CenterZ=0 NormalX=0 NormalY=0 NormalZ=1 AngleXU=0 Radius=1
    g328: Circle CenterX=-1.92719 CenterY=-91.7794 CenterZ=0 NormalX=0 NormalY=0 NormalZ=1 AngleXU=0 Radius=1
    g329: Circle CenterX=1.57905 CenterY=-89.8542 CenterZ=0 NormalX=0 NormalY=0 NormalZ=1 AngleXU=0 Radius=1
    g330: BSplineCurve PolesCount=3 KnotsCount=2 Degree=2 IsPeriodic=0
    g331: GeomPoint X=2.07281 Y=-91.7794 Z=0
    g332: GeomPoint X=1.57905 Y=-89.8542 Z=0
    g333: LineSegment StartX=2.07281 StartY=-91.7794 StartZ=0 EndX=42.0728 EndY=-91.7794 EndZ=0
    g334: LineSegment StartX=46.0728 StartY=-87.7794 StartZ=0 EndX=46.0728 EndY=-69.424 EndZ=0
    g335: LineSegment StartX=42.5666 StartY=-67.3492 StartZ=0 EndX=1.57905 EndY=-89.8542 EndZ=0
    g336: Circle CenterX=322.073 CenterY=76.4095 CenterZ=0 NormalX=0 NormalY=0 NormalZ=1 AngleXU=0 Radius=4
    g337: BSplineCurve PolesCount=3 KnotsCount=2 Degree=2 IsPeriodic=0
    g338: GeomPoint X=318.073 Y=72.4095 Z=0
    g339: GeomPoint X=322.073 Y=76.4095 Z=0
    g340: Circle CenterX=375.073 CenterY=72.4095 CenterZ=0 NormalX=0 NormalY=0 NormalZ=1 AngleXU=0 Radius=1
    g341: Circle CenterX=375.073 CenterY=76.4095 CenterZ=0 NormalX=0 NormalY=0 NormalZ=1 AngleXU=0 Radius=1
    g342: Circle CenterX=371.073 CenterY=76.4095 CenterZ=0 NormalX=0 NormalY=0 NormalZ=1 AngleXU=0 Radius=1
    g343: BSplineCurve PolesCount=3 KnotsCount=2 Degree=2 IsPeriodic=0
    g344: GeomPoint X=375.073 Y=72.4095 Z=0
    g345: GeomPoint X=371.073 Y=76.4095 Z=0
    g346: LineSegment StartX=322.073 StartY=76.4095 StartZ=0 EndX=371.073 EndY=76.4095 EndZ=0
    g347: LineSegment StartX=318.073 StartY=72.4095 StartZ=0 EndX=318.073 EndY=-47.4823 EndZ=0
    g348: LineSegment StartX=375.073 StartY=72.4095 StartZ=0 EndX=375.073 EndY=-78.7896 EndZ=0
    g349: LineSegment StartX=-18.9272 StartY=22.1087 StartZ=0 EndX=-22.9272 EndY=22.1087 EndZ=0
    g350: LineSegment StartX=-34.9272 StartY=22.1087 StartZ=0 EndX=-30.9272 EndY=22.1087 EndZ=0
    g351: ArcOfCircle CenterX=-26.9272 CenterY=22.1087 CenterZ=0 NormalX=0 NormalY=0 NormalZ=1 AngleXU=0 Radius=4 StartAngle=8.3e-15 EndAngle=3.14159
  constraints (584):
    c: Coincident(g0,g2)
    c: Block(g0)
    c: Block(g1)
    c: Vertical(g3)
    c: Vertical(g4)
    c: Block(g4)
    c: Block(g3)
    c: Tangent(g5,g8) = 1.5708
    c: Tangent(g5,g7) = -1.5708
    c: Tangent(g7,g6) = -1.5708
    c: Tangent(g8,g6) = 1.5708
    c: Vertical(g7)
    c: Equal(g5,g6)
    c: Block(g8)
    c: Block(g7)
    c: Tangent(g9,g10) = 1.5708
    c: Tangent(g10,g12) = 1.5708
    c: Equal(g9,g12)
    c: Coincident(g11,g9)
    c: Coincident(g11,g12)
    c: Block(g10)
    c: Block(g11)
    c: Weight(g13) = 1
    c: Equal(g13,g14)
    c: Equal(g13,g15)
    c: InternalAlignment(g13,g16)
    c: InternalAlignment(g14,g16)
    c: InternalAlignment(g15,g16)
    c: InternalAlignment(g17,g16)
    c: InternalAlignment(g18,g16)
    c: Weight(g19) = 1
    c: Equal(g19,g20)
    c: Equal(g19,g21)
    c: InternalAlignment(g19,g22)
    c: InternalAlignment(g20,g22)
    c: InternalAlignment(g21,g22)
    c: InternalAlignment(g23,g22)
    c: InternalAlignment(g24,g22)
    c: Block(g22)
    c: Block(g16)
    c: Weight(g25) = 1
    c: Equal(g25,g26)
    c: Equal(g25,g27)
    c: InternalAlignment(g25,g28)
    c: InternalAlignment(g26,g28)
    c: InternalAlignment(g27,g28)
    c: InternalAlignment(g29,g28)
    c: InternalAlignment(g30,g28)
    c: Weight(g31) = 1
    c: Equal(g31,g32)
    c: Equal(g31,g33)
    c: InternalAlignment(g31,g34)
    c: InternalAlignment(g32,g34)
    c: InternalAlignment(g33,g34)
    c: InternalAlignment(g35,g34)
    c: InternalAlignment(g36,g34)
    c: Block(g34)
    c: Block(g28)
    c: Weight(g37) = 1
    c: Equal(g37,g38)
    c: Equal(g37,g39)
    c: InternalAlignment(g37,g40)
    c: InternalAlignment(g38,g40)
    c: InternalAlignment(g39,g40)
    c: InternalAlignment(g41,g40)
    c: InternalAlignment(g42,g40)
    c: Weight(g43) = 1
    c: Equal(g43,g44)
    c: Equal(g43,g45)
    c: InternalAlignment(g43,g46)
    c: InternalAlignment(g44,g46)
    c: InternalAlignment(g45,g46)
    c: InternalAlignment(g47,g46)
    c: InternalAlignment(g48,g46)
    c: Block(g40)
    c: Block(g46)
    c: Coincident(g49,g4)
    c: Coincident(g49,g3)
    c: Horizontal(g49)
    c: Distance(g49) = 450
    c: Coincident(g50,g4)
    c: Coincident(g50,g3)
    c: Horizontal(g50)
    c: Horizontal(g51)
    c: Coincident(g2,g51)
    c: Block(g51)
    c: Coincident(g1,g51)
    c: Weight(g52) = 1
    c: Equal(g52,g53)
    c: Equal(g52,g54)
    c: InternalAlignment(g52,g55)
    c: InternalAlignment(g53,g55)
    c: InternalAlignment(g54,g55)
    c: InternalAlignment(g56,g55)
    c: InternalAlignment(g57,g55)
    c: Block(g55)
    c: Weight(g58) = 1
    c: Equal(g58,g59)
    c: Equal(g58,g60)
    c: InternalAlignment(g58,g61)
    c: InternalAlignment(g59,g61)
    c: InternalAlignment(g60,g61)
    c: InternalAlignment(g62,g61)
    c: InternalAlignment(g63,g61)
    c: Block(g61)
    c: Weight(g64) = 1
    c: Equal(g64,g65)
    c: Equal(g64,g66)
    c: InternalAlignment(g64,g67)
    c: InternalAlignment(g65,g67)
    c: InternalAlignment(g66,g67)
    c: InternalAlignment(g68,g67)
    c: InternalAlignment(g69,g67)
    c: Block(g67)
    c: Weight(g70) = 1
    c: Equal(g70,g71)
    c: Equal(g70,g72)
    c: InternalAlignment(g70,g73)
    c: InternalAlignment(g71,g73)
    c: InternalAlignment(g72,g73)
    c: InternalAlignment(g74,g73)
    c: InternalAlignment(g75,g73)
    c: Block(g73)
    c: Weight(g76) = 1
    c: Equal(g76,g77)
    c: Equal(g76,g78)
    c: InternalAlignment(g76,g79)
    c: InternalAlignment(g77,g79)
    c: InternalAlignment(g78,g79)
    c: InternalAlignment(g80,g79)
    c: InternalAlignment(g81,g79)
    c: Weight(g82) = 1
    c: Equal(g82,g83)
    c: Equal(g82,g84)
    c: InternalAlignment(g82,g85)
    c: InternalAlignment(g83,g85)
    c: InternalAlignment(g84,g85)
    c: InternalAlignment(g86,g85)
    c: InternalAlignment(g87,g85)
    c: Block(g79)
    c: Block(g85)
    c: Coincident(g88,g79)
    c: Coincident(g88,g85)
    c: Vertical(g88)
    c: Coincident(g89,g79)
    c: Coincident(g89,g61)
    c: Coincident(g90,g61)
    c: Coincident(g90,g85)
    c: Weight(g91) = 1
    c: Equal(g91,g92)
    c: Equal(g91,g93)
    c: InternalAlignment(g91,g94)
    c: InternalAlignment(g92,g94)
    c: InternalAlignment(g93,g94)
    c: InternalAlignment(g95,g94)
    c: InternalAlignment(g96,g94)
    c: Weight(g97) = 1
    c: Equal(g97,g98)
    c: Equal(g97,g99)
    c: InternalAlignment(g97,g100)
    c: InternalAlignment(g98,g100)
    c: InternalAlignment(g99,g100)
    c: InternalAlignment(g101,g100)
    c: InternalAlignment(g102,g100)
    c: Block(g94)
    c: Block(g100)
    c: Coincident(g103,g94)
    c: Coincident(g103,g100)
    c: Vertical(g103)
    c: Coincident(g104,g94)
    c: Coincident(g104,g55)
    c: Coincident(g105,g55)
    c: Coincident(g105,g100)
    c: Weight(g106) = 1
    c: Equal(g106,g107)
    c: Equal(g106,g108)
    c: InternalAlignment(g106,g109)
    c: InternalAlignment(g107,g109)
    c: InternalAlignment(g108,g109)
    c: InternalAlignment(g110,g109)
    c: InternalAlignment(g111,g109)
    c: Weight(g112) = 1
    c: Equal(g112,g113)
    c: Equal(g112,g114)
    c: InternalAlignment(g112,g115)
    c: InternalAlignment(g113,g115)
    c: InternalAlignment(g114,g115)
    c: InternalAlignment(g116,g115)
    c: InternalAlignment(g117,g115)
    c: Block(g109)
    c: Block(g115)
    c: Coincident(g118,g109)
    c: Coincident(g118,g115)
    c: Vertical(g118)
    c: Coincident(g119,g115)
    c: Coincident(g119,g73)
    c: Coincident(g120,g73)
    c: Coincident(g120,g109)
    c: Weight(g121) = 1
    c: Equal(g121,g122)
    c: Equal(g121,g123)
    c: InternalAlignment(g121,g124)
    c: InternalAlignment(g122,g124)
    c: InternalAlignment(g123,g124)
    c: InternalAlignment(g125,g124)
    c: InternalAlignment(g126,g124)
    c: Weight(g127) = 1
    c: Equal(g127,g128)
    c: Equal(g127,g129)
    c: InternalAlignment(g127,g130)
    c: InternalAlignment(g128,g130)
    c: InternalAlignment(g129,g130)
    c: InternalAlignment(g131,g130)
    c: InternalAlignment(g132,g130)
    c: Block(g124)
    c: Block(g130)
    c: Coincident(g133,g124)
    c: Coincident(g133,g130)
    c: Vertical(g133)
    c: Coincident(g134,g130)
    c: Coincident(g134,g67)
    c: Coincident(g135,g67)
    c: Coincident(g135,g124)
    c: Weight(g136) = 1
    c: Equal(g136,g137)
    c: Equal(g136,g138)
    c: InternalAlignment(g136,g139)
    c: InternalAlignment(g137,g139)
    c: InternalAlignment(g138,g139)
    c: InternalAlignment(g140,g139)
    c: InternalAlignment(g141,g139)
    c: Weight(g142) = 1
    c: Equal(g142,g143)
    c: Equal(g142,g144)
    c: InternalAlignment(g142,g145)
    c: InternalAlignment(g143,g145)
    c: InternalAlignment(g144,g145)
    c: InternalAlignment(g146,g145)
    c: InternalAlignment(g147,g145)
    c: Weight(g148) = 1
    c: Equal(g148,g149)
    c: Equal(g148,g150)
    c: InternalAlignment(g148,g151)
    c: InternalAlignment(g149,g151)
    c: InternalAlignment(g150,g151)
    c: InternalAlignment(g152,g151)
    c: InternalAlignment(g153,g151)
    c: Weight(g154) = 1
    c: Equal(g154,g155)
    c: Equal(g154,g156)
    c: InternalAlignment(g154,g157)
    c: InternalAlignment(g155,g157)
    c: InternalAlignment(g156,g157)
    c: InternalAlignment(g158,g157)
    c: InternalAlignment(g159,g157)
    c: Block(g157)
    c: Block(g151)
    c: Block(g145)
    c: Block(g139)
    c: Coincident(g160,g34)
    c: Coincident(g160,g157)
    c: Coincident(g161,g157)
    c: Coincident(g161,g151)
    c: Horizontal(g161)
    c: Coincident(g162,g151)
    c: Coincident(g162,g34)
    c: Vertical(g162)
    c: Coincident(g163,g28)
    c: Coincident(g163,g145)
    c: Vertical(g163)
    c: Coincident(g164,g145)
    c: Coincident(g164,g139)
    c: Horizontal(g164)
    c: Coincident(g165,g139)
    c: Coincident(g165,g28)
    c: Weight(g166) = 1
    c: Equal(g166,g167)
    c: Equal(g166,g168)
    c: InternalAlignment(g166,g169)
    c: InternalAlignment(g167,g169)
    c: InternalAlignment(g168,g169)
    c: InternalAlignment(g170,g169)
    c: InternalAlignment(g171,g169)
    c: Weight(g172) = 1
    c: Equal(g172,g173)
    c: Equal(g172,g174)
    c: InternalAlignment(g172,g175)
    c: InternalAlignment(g173,g175)
    c: InternalAlignment(g174,g175)
    c: InternalAlignment(g176,g175)
    c: InternalAlignment(g177,g175)
    c: Weight(g178) = 1
    c: Equal(g178,g179)
    c: Equal(g178,g180)
    c: InternalAlignment(g178,g181)
    c: InternalAlignment(g179,g181)
    c: InternalAlignment(g180,g181)
    c: InternalAlignment(g182,g181)
    c: InternalAlignment(g183,g181)
    c: Weight(g184) = 1
    c: Equal(g184,g185)
    c: Equal(g184,g186)
    c: InternalAlignment(g184,g187)
    c: InternalAlignment(g185,g187)
    c: InternalAlignment(g186,g187)
    c: InternalAlignment(g188,g187)
    c: InternalAlignment(g189,g187)
    c: Block(g187)
    c: Block(g181)
    c: Block(g175)
    c: Block(g169)
    c: Coincident(g190,g187)
    c: Coincident(g190,g181)
    c: Horizontal(g190)
    c: Coincident(g191,g181)
    c: Coincident(g191,g16)
    c: Vertical(g191)
    c: Coincident(g192,g22)
    c: Coincident(g192,g175)
    c: Vertical(g192)
    c: Coincident(g193,g175)
    c: Coincident(g193,g169)
    c: Horizontal(g193)
    c: Coincident(g194,g169)
    c: Coincident(g194,g22)
    c: Coincident(g195,g16)
    c: Weight(g196) = 1
    c: Equal(g196,g197)
    c: Equal(g196,g198)
    c: InternalAlignment(g196,g199)
    c: InternalAlignment(g197,g199)
    c: InternalAlignment(g198,g199)
    c: InternalAlignment(g200,g199)
    c: InternalAlignment(g201,g199)
    c: Weight(g202) = 1
    c: Equal(g202,g203)
    c: Equal(g202,g204)
    c: InternalAlignment(g202,g205)
    c: InternalAlignment(g203,g205)
    c: InternalAlignment(g204,g205)
    c: InternalAlignment(g206,g205)
    c: InternalAlignment(g207,g205)
    c: Block(g205)
    c: Block(g199)
    c: Coincident(g208,g205)
    c: Coincident(g208,g40)
    c: Coincident(g209,g40)
    c: Coincident(g209,g199)
    c: Coincident(g210,g199)
    c: Coincident(g210,g205)
    c: Vertical(g210)
    c: Weight(g211) = 1
    c: Equal(g211,g212)
    c: Equal(g211,g213)
    c: InternalAlignment(g211,g214)
    c: InternalAlignment(g212,g214)
    c: InternalAlignment(g213,g214)
    c: InternalAlignment(g215,g214)
    c: InternalAlignment(g216,g214)
    c: Weight(g217) = 1
    c: Equal(g217,g218)
    c: Equal(g217,g219)
    c: InternalAlignment(g217,g220)
    c: InternalAlignment(g218,g220)
    c: InternalAlignment(g219,g220)
    c: InternalAlignment(g221,g220)
    c: InternalAlignment(g222,g220)
    c: Block(g220)
    c: Block(g214)
    c: Coincident(g223,g214)
    c: Coincident(g223,g46)
    c: Coincident(g224,g46)
    c: Coincident(g224,g220)
    c: Coincident(g225,g220)
    c: Coincident(g225,g214)
    c: Vertical(g225)
    c: Horizontal(g226)
    c: Block(g226)
    c: Vertical(g227)
    c: Block(g227)
    c: Block(g228)
    c: Weight(g229) = 1
    c: Equal(g229,g230)
    c: Equal(g229,g231)
    c: InternalAlignment(g229,g232)
    c: InternalAlignment(g230,g232)
    c: InternalAlignment(g231,g232)
    c: InternalAlignment(g233,g232)
    c: InternalAlignment(g234,g232)
    c: Weight(g235) = 1
    c: Equal(g235,g236)
    c: Equal(g235,g237)
    c: InternalAlignment(g235,g238)
    c: InternalAlignment(g236,g238)
    c: InternalAlignment(g237,g238)
    c: InternalAlignment(g239,g238)
    c: InternalAlignment(g240,g238)
    c: Weight(g241) = 1
    c: Equal(g241,g242)
    c: Equal(g241,g243)
    c: InternalAlignment(g241,g244)
    c: InternalAlignment(g242,g244)
    c: InternalAlignment(g243,g244)
    c: InternalAlignment(g245,g244)
    c: InternalAlignment(g246,g244)
    c: Weight(g247) = 1
    c: Equal(g247,g248)
    c: Equal(g247,g249)
    c: InternalAlignment(g247,g250)
    c: InternalAlignment(g248,g250)
    c: InternalAlignment(g249,g250)
    c: InternalAlignment(g251,g250)
    c: InternalAlignment(g252,g250)
    c: Block(g232)
    c: Block(g238)
    c: Block(g244)
    c: Block(g250)
    c: Coincident(g253,g238)
    c: Coincident(g253,g232)
    c: Horizontal(g253)
    c: Block(g195)
    c: Weight(g254) = 1
    c: Equal(g254,g255)
    c: Equal(g254,g256)
    c: InternalAlignment(g254,g257)
    c: InternalAlignment(g255,g257)
    c: InternalAlignment(g256,g257)
    c: InternalAlignment(g258,g257)
    c: InternalAlignment(g259,g257)
    c: Weight(g260) = 1
    c: Equal(g260,g261)
    c: Equal(g260,g262)
    c: InternalAlignment(g260,g263)
    c: InternalAlignment(g261,g263)
    c: InternalAlignment(g262,g263)
    c: InternalAlignment(g264,g263)
    c: InternalAlignment(g265,g263)
    c: Block(g257)
    c: Block(g263)
    c: Coincident(g266,g257)
    c: Coincident(g266,g263)
    c: Weight(g267) = 1
    c: Equal(g267,g268)
    c: Equal(g267,g269)
    c: InternalAlignment(g267,g270)
    c: InternalAlignment(g268,g270)
    c: InternalAlignment(g269,g270)
    c: InternalAlignment(g271,g270)
    c: InternalAlignment(g272,g270)
    c: Weight(g273) = 1
    c: Equal(g273,g274)
    c: Equal(g273,g275)
    c: InternalAlignment(g273,g276)
    c: InternalAlignment(g274,g276)
    c: InternalAlignment(g275,g276)
    c: InternalAlignment(g277,g276)
    c: InternalAlignment(g278,g276)
    c: Weight(g279) = 1
    c: Equal(g279,g280)
    c: Equal(g279,g281)
    c: InternalAlignment(g279,g282)
    c: InternalAlignment(g280,g282)
    c: InternalAlignment(g281,g282)
    c: InternalAlignment(g283,g282)
    c: InternalAlignment(g284,g282)
    c: Block(g282)
    c: Block(g276)
    c: Block(g270)
    c: Coincident(g285,g276)
    c: Coincident(g285,g270)
    c: Coincident(g286,g270)
    c: Coincident(g286,g282)
    c: Vertical(g286)
    c: Coincident(g287,g282)
    c: Coincident(g287,g276)
    c: Horizontal(g287)
    c: Weight(g288) = 1
    c: Equal(g288,g289)
    c: InternalAlignment(g288,g290)
    c: InternalAlignment(g289,g290)
    c: InternalAlignment(g291,g290)
    c: InternalAlignment(g292,g290)
    c: Weight(g293) = 1
    c: Equal(g293,g294)
    c: Equal(g293,g295)
    c: InternalAlignment(g294,g296)
    c: InternalAlignment(g295,g296)
    c: InternalAlignment(g297,g296)
    c: InternalAlignment(g298,g296)
    c: Weight(g299) = 1
    c: Equal(g299,g300)
    c: Equal(g299,g301)
    c: InternalAlignment(g299,g302)
    c: InternalAlignment(g300,g302)
    c: InternalAlignment(g301,g302)
    c: InternalAlignment(g303,g302)
    c: InternalAlignment(g304,g302)
    c: Equal(g305,g306)
    c: Equal(g305,g307)
    c: InternalAlignment(g305,g308)
    c: InternalAlignment(g306,g308)
    c: InternalAlignment(g307,g308)
    c: InternalAlignment(g309,g308)
    c: InternalAlignment(g310,g308)
    c: Block(g296)
    c: Block(g302)
    c: Block(g308)
    c: Block(g290)
    c: Coincident(g311,g290)
    c: Coincident(g311,g296)
    c: Horizontal(g311)
    c: Coincident(g312,g296)
    c: Coincident(g312,g302)
    c: Vertical(g312)
    c: Coincident(g313,g302)
    c: Coincident(g313,g308)
    c: Horizontal(g313)
    c: Coincident(g314,g308)
    c: Coincident(g314,g290)
    c: Weight(g315) = 1
    c: Equal(g315,g316)
    c: Equal(g315,g317)
    c: InternalAlignment(g315,g318)
    c: InternalAlignment(g316,g318)
    c: InternalAlignment(g317,g318)
    c: InternalAlignment(g319,g318)
    c: InternalAlignment(g320,g318)
    c: Weight(g321) = 1
    c: Equal(g321,g322)
    c: Equal(g321,g323)
    c: InternalAlignment(g321,g324)
    c: InternalAlignment(g322,g324)
    c: InternalAlignment(g323,g324)
    c: InternalAlignment(g325,g324)
    c: InternalAlignment(g326,g324)
    c: Weight(g327) = 1
    c: Equal(g327,g328)
    c: Equal(g327,g329)
    c: InternalAlignment(g327,g330)
    c: InternalAlignment(g328,g330)
    c: InternalAlignment(g329,g330)
    c: InternalAlignment(g331,g330)
    c: InternalAlignment(g332,g330)
    c: Block(g330)
    c: Block(g324)
    c: Block(g318)
    c: Coincident(g333,g330)
    c: Coincident(g333,g324)
    c: Horizontal(g333)
    c: Coincident(g334,g324)
    c: Coincident(g334,g318)
    c: Vertical(g334)
    c: Coincident(g335,g318)
    c: Coincident(g335,g330)
    c: InternalAlignment(g336,g337)
    c: InternalAlignment(g338,g337)
    c: InternalAlignment(g339,g337)
    c: Block(g337)
    c: Equal(g340,g341)
    c: Equal(g340,g342)
    c: InternalAlignment(g340,g343)
    c: InternalAlignment(g341,g343)
    c: InternalAlignment(g342,g343)
    c: InternalAlignment(g344,g343)
    c: InternalAlignment(g345,g343)
    c: Block(g343)
    c: Coincident(g346,g337)
    c: Horizontal(g346)
    c: Block(g346)
    c: Coincident(g347,g337)
    c: Coincident(g347,g263)
    c: Vertical(g347)
    c: Coincident(g348,g343)
    c: Coincident(g348,g257)
    c: Vertical(g348)
    c: Coincident(g349,g5)
    c: Horizontal(g349)
    c: Coincident(g350,g5)
    c: Horizontal(g350)
    c: Distance(g350) = 4
    c: Distance(g349) = 4
    c: Coincident(g351,g5)
    c: Coincident(g351,g349)
    c: Coincident(g351,g350)
FEATURE [Sketcher::SketchObject] Sketch001
  FullyConstrained = true
  MapMode = 4
  Placement = pos=(0,0,0) rot=(0.57735,0.57735,0.57735;2.0944rad)
  Support = -> [Sketch]
  sketch-geometry (46):
    g0: BSplineCurve PolesCount=3 KnotsCount=2 Degree=2 IsPeriodic=0
    g1: ArcOfCircle CenterX=73.1223 CenterY=-32.291 CenterZ=0 NormalX=0 NormalY=0 NormalZ=1 AngleXU=0 Radius=13 StartAngle=5.92268 EndAngle=9.06428
    g2: ArcOfCircle CenterX=66.7816 CenterY=-49.1439 CenterZ=0 NormalX=0 NormalY=0 NormalZ=1 AngleXU=0 Radius=13 StartAngle=2.78068 EndAngle=5.92131
    g3: ArcOfCircle CenterX=55.9263 CenterY=-78.1807 CenterZ=0 NormalX=0 NormalY=0 NormalZ=1 AngleXU=0 Radius=13 StartAngle=5.92268 EndAngle=9.06428
    g4: ArcOfCircle CenterX=49.5884 CenterY=-95.0342 CenterZ=0 NormalX=0 NormalY=0 NormalZ=1 AngleXU=0 Radius=13 StartAngle=2.78068 EndAngle=5.92131
    g5: ArcOfCircle CenterX=38.7206 CenterY=-124.067 CenterZ=0 NormalX=0 NormalY=0 NormalZ=1 AngleXU=0 Radius=13 StartAngle=5.92268 EndAngle=9.06428
    g6: ArcOfCircle CenterX=32.3875 CenterY=-140.92 CenterZ=0 NormalX=0 NormalY=0 NormalZ=1 AngleXU=0 Radius=13 StartAngle=2.78068 EndAngle=5.92131
    g7: ArcOfCircle CenterX=21.4715 CenterY=-169.934 CenterZ=0 NormalX=0 NormalY=0 NormalZ=1 AngleXU=0 Radius=13 StartAngle=5.92268 EndAngle=9.06428
    g8: ArcOfCircle CenterX=15.1336 CenterY=-186.787 CenterZ=0 NormalX=0 NormalY=0 NormalZ=1 AngleXU=0 Radius=13 StartAngle=2.78068 EndAngle=5.92131
    g9-g12: Circle x4 (B-spline internal-alignment scaffolding for g13; pole/knot coordinates omitted)
    g13: BSplineCurve PolesCount=4 KnotsCount=2 Degree=3 IsPeriodic=0
    g14: GeomPoint X=28.8094 Y=-19.0875 Z=0
    g15: GeomPoint X=47.0443 Y=-50.4712 Z=0
    g16: Circle CenterX=53.5586 CenterY=-23.2695 CenterZ=0 NormalX=0 NormalY=0 NormalZ=1 AngleXU=0 Radius=3.24518
    g17: Circle CenterX=-195.441 CenterY=-127.082 CenterZ=0 NormalX=0 NormalY=0 NormalZ=1 AngleXU=0 Radius=1
    g18: Circle CenterX=-8.24091 CenterY=-197.481 CenterZ=0 NormalX=0 NormalY=0 NormalZ=1 AngleXU=0 Radius=1
    g19: Circle CenterX=12.8789 CenterY=-141.321 CenterZ=0 NormalX=0 NormalY=0 NormalZ=1 AngleXU=0 Radius=1
    g20: BSplineCurve PolesCount=3 KnotsCount=2 Degree=2 IsPeriodic=0
    g21: GeomPoint X=-195.441 Y=-127.082 Z=0
    g22: GeomPoint X=12.8789 Y=-141.321 Z=0
    g23: Circle CenterX=-12.8016 CenterY=-179.036 CenterZ=0 NormalX=0 NormalY=0 NormalZ=1 AngleXU=0 Radius=10.5072
    g24: Circle CenterX=0.933922 CenterY=-166.43 CenterZ=0 NormalX=0 NormalY=0 NormalZ=1 AngleXU=0 Radius=3.26661
    g25: Circle CenterX=-33.5518 CenterY=-176.44 CenterZ=0 NormalX=0 NormalY=0 NormalZ=1 AngleXU=0 Radius=5.64388
    g26: Circle CenterX=-47.2366 CenterY=-173.859 CenterZ=0 NormalX=0 NormalY=0 NormalZ=1 AngleXU=0 Radius=3.01653
    g27: Circle CenterX=-56.2595 CenterY=-171.456 CenterZ=0 NormalX=0 NormalY=0 NormalZ=1 AngleXU=0 Radius=2.12826
    g28: ArcOfCircle CenterX=51.2151 CenterY=-198.473 CenterZ=0 NormalX=0 NormalY=0 NormalZ=1 AngleXU=0 Radius=20 StartAngle=2.78189 EndAngle=4.35269
    g29: LineSegment StartX=32.4951 StartY=-191.433 StartZ=0 EndX=94.6578 EndY=-26.1352 EndZ=0
    g30: LineSegment StartX=43.1192 StartY=-220.001 StartZ=0 EndX=-196.497 EndY=-129.89 EndZ=0
    g31: LineSegment StartX=43.1192 StartY=-220.001 StartZ=0 EndX=44.1752 EndY=-217.193 EndZ=0
    g32: LineSegment StartX=117.223 StartY=-19.0875 StartZ=0 EndX=117.223 EndY=-16.0875 EndZ=0
    g33: LineSegment StartX=117.223 StartY=-16.0875 StartZ=0 EndX=17.2232 EndY=-16.0875 EndZ=0
    g34: LineSegment StartX=17.2232 StartY=-16.0875 StartZ=0 EndX=17.2232 EndY=-19.0875 EndZ=0
    g35: LineSegment StartX=28.8094 StartY=-19.0875 StartZ=0 EndX=17.2232 EndY=-19.0875 EndZ=0
    g36: LineSegment StartX=47.0443 StartY=-50.4712 StartZ=0 EndX=12.8789 EndY=-141.321 EndZ=0
    g37: LineSegment StartX=-195.441 StartY=-127.082 StartZ=0 EndX=-196.497 EndY=-129.89 EndZ=0
    g38: LineSegment StartX=85.2866 StartY=-36.8766 StartZ=0 EndX=78.9396 EndY=-53.7463 EndZ=0
    g39: LineSegment StartX=60.9579 StartY=-27.7053 StartZ=0 EndX=54.6191 EndY=-44.5532 EndZ=0
    g40: LineSegment StartX=68.0907 StartY=-82.7664 StartZ=0 EndX=61.7465 EndY=-99.6365 EndZ=0
    g41: LineSegment StartX=43.7619 StartY=-73.595 StartZ=0 EndX=37.426 EndY=-90.4435 EndZ=0
    g42: LineSegment StartX=50.885 StartY=-128.652 StartZ=0 EndX=44.5456 EndY=-145.522 EndZ=0
    g43: LineSegment StartX=26.5562 StartY=-119.481 StartZ=0 EndX=20.2251 EndY=-136.329 EndZ=0
    g44: LineSegment StartX=9.3071 StartY=-165.349 StartZ=0 EndX=2.97115 EndY=-182.197 EndZ=0
    g45: LineSegment StartX=33.6358 StartY=-174.52 StartZ=0 EndX=27.2917 EndY=-191.39 EndZ=0
  constraints (71):
    c: Block(g0)
    c: Block(g1)
    c: Block(g2)
    c: Block(g4)
    c: Block(g3)
    c: Block(g6)
    c: Block(g5)
    c: Block(g8)
    c: Block(g7)
    c: Weight(g9) = 1
    c: Equal(g9,g10)
    c: Equal(g9,g11)
    c: Equal(g9,g12)
    c: InternalAlignment(g9-g12 -> g13) x4
    c: InternalAlignment(g14,g13)
    c: InternalAlignment(g15,g13)
    c: Block(g16)
    c: Weight(g17) = 1
    c: Equal(g17,g18)
    c: Equal(g17,g19)
    c: InternalAlignment(g17,g20)
    c: InternalAlignment(g18,g20)
    c: InternalAlignment(g19,g20)
    c: InternalAlignment(g21,g20)
    c: InternalAlignment(g22,g20)
    c: Block(g20)
    c: Block(g23)
    c: Block(g24)
    c: Block(g25)
    c: Block(g26)
    c: Block(g27)
    c: Block(g28)
    c: Coincident(g29,g28)
    c: Coincident(g29,g0)
    c: Block(g13)
    c: Coincident(g31,g30)
    c: Coincident(g31,g28)
    c: Block(g31)
    c: Coincident(g32,g0)
    c: Vertical(g32)
    c: Coincident(g33,g32)
    c: Horizontal(g33)
    c: Coincident(g34,g33)
    c: Vertical(g34)
    c: Block(g33)
    c: Coincident(g35,g13)
    c: Coincident(g35,g34)
    c: Horizontal(g35)
    c: Coincident(g36,g13)
    c: Coincident(g36,g20)
    c: Coincident(g37,g20)
    c: Coincident(g37,g30)
    c: Block(g30)
    c: Coincident(g38,g1)
    c: Coincident(g38,g2)
    c: Coincident(g39,g1)
    c: Coincident(g39,g2)
    c: Coincident(g40,g3)
    c: Coincident(g40,g4)
    c: Coincident(g41,g3)
    c: Coincident(g41,g4)
    c: Coincident(g42,g5)
    c: Coincident(g42,g6)
    c: Coincident(g43,g5)
    c: Coincident(g43,g6)
    c: Coincident(g44,g7)
    c: Coincident(g44,g8)
    c: Coincident(g45,g7)
    c: Coincident(g45,g8)
    c: Distance(g30) = 256
    c: Distance(g33) = 100
FEATURE [Part::Extrusion] Extrude002
  Base = -> Sketch001
  Dir = (1,0,0)
  DirMode = 2
  FaceMakerClass = Part::FaceMakerBullseye
  LengthFwd = 8
  LengthRev = 0
  Solid = true
  Symmetric = false
FEATURE [Sketcher::SketchObject] Sketch002
  FullyConstrained = true
  sketch-geometry (20):
    g0: LineSegment StartX=-2.77179 StartY=-200.304 StartZ=0 EndX=5.22821 EndY=-200.304 EndZ=0
    g1: LineSegment StartX=5.22821 StartY=-200.304 StartZ=0 EndX=5.22821 EndY=-197.304 EndZ=0
    g2: LineSegment StartX=-2.77179 StartY=-200.304 StartZ=0 EndX=-2.77179 EndY=-197.304 EndZ=0
    g3: LineSegment StartX=5.22821 StartY=-197.304 StartZ=0 EndX=8.22821 EndY=-197.304 EndZ=0
    g4: LineSegment StartX=-2.77179 StartY=-197.304 StartZ=0 EndX=-5.77179 EndY=-197.304 EndZ=0
    g5: LineSegment StartX=19.2282 StartY=-203.304 StartZ=0 EndX=19.2282 EndY=-206.304 EndZ=0
    g6: LineSegment StartX=-16.7718 StartY=-203.304 StartZ=0 EndX=-16.7718 EndY=-206.304 EndZ=0
    g7: LineSegment StartX=-16.7718 StartY=-206.304 StartZ=0 EndX=19.2282 EndY=-206.304 EndZ=0
    g8: Circle CenterX=-16.7718 CenterY=-203.304 CenterZ=0 NormalX=0 NormalY=0 NormalZ=1 AngleXU=0 Radius=1
    g9: Circle CenterX=-5.77179 CenterY=-203.304 CenterZ=0 NormalX=0 NormalY=0 NormalZ=1 AngleXU=0 Radius=1
    g10: Circle CenterX=-5.77179 CenterY=-197.304 CenterZ=0 NormalX=0 NormalY=0 NormalZ=1 AngleXU=0 Radius=1
    g11: BSplineCurve PolesCount=3 KnotsCount=2 Degree=2 IsPeriodic=0
    g12: GeomPoint X=-16.7718 Y=-203.304 Z=0
    g13: GeomPoint X=-5.77179 Y=-197.304 Z=0
    g14: Circle CenterX=19.2282 CenterY=-203.304 CenterZ=0 NormalX=0 NormalY=0 NormalZ=1 AngleXU=0 Radius=1
    g15: Circle CenterX=8.22821 CenterY=-203.304 CenterZ=0 NormalX=0 NormalY=0 NormalZ=1 AngleXU=0 Radius=1
    g16: Circle CenterX=8.22821 CenterY=-197.304 CenterZ=0 NormalX=0 NormalY=0 NormalZ=1 AngleXU=0 Radius=1
    g17: BSplineCurve PolesCount=3 KnotsCount=2 Degree=2 IsPeriodic=0
    g18: GeomPoint X=19.2282 Y=-203.304 Z=0
    g19: GeomPoint X=8.22821 Y=-197.304 Z=0
  constraints (41):
    c: Horizontal(g0)
    c: Distance(g0) = 8
    c: Coincident(g1,g0)
    c: Vertical(g1)
    c: Distance(g1) = 3
    c: Coincident(g2,g0)
    c: Vertical(g2)
    c: Distance(g2) = 3
    c: Coincident(g3,g1)
    c: Horizontal(g3)
    c: Distance(g3) = 3
    c: Coincident(g4,g2)
    c: Horizontal(g4)
    c: Distance(g4) = 3
    c: Vertical(g5)
    c: Vertical(g6)
    c: Coincident(g7,g6)
    c: Coincident(g7,g5)
    c: Weight(g8) = 1
    c: Equal(g8,g9)
    c: Equal(g8,g10)
    c: Coincident(g11,g4)
    c: InternalAlignment(g8,g11)
    c: InternalAlignment(g9,g11)
    c: InternalAlignment(g10,g11)
    c: InternalAlignment(g12,g11)
    c: InternalAlignment(g13,g11)
    c: Coincident(g17,g5)
    c: Weight(g14) = 1
    c: Equal(g14,g15)
    c: Equal(g14,g16)
    c: Coincident(g17,g3)
    c: InternalAlignment(g14,g17)
    c: InternalAlignment(g15,g17)
    c: InternalAlignment(g16,g17)
    c: InternalAlignment(g18,g17)
    c: InternalAlignment(g19,g17)
    c: Block(g7)
    c: Block(g17)
    c: Block(g11)
    c: Block(g6)
FEATURE [Part::Extrusion] Extrude003
  Base = -> Sketch002
  Dir = (0,0,1)
  DirMode = 2
  FaceMakerClass = Part::FaceMakerBullseye
  LengthFwd = 260
  LengthRev = 0
  Solid = true
  Symmetric = false
FEATURE [Part::Extrusion] Extrude
  Base = -> Sketch
  Dir = (0,0,1)
  DirMode = 2
  FaceMakerClass = Part::FaceMakerBullseye
  LengthFwd = 14
  LengthRev = 0
  Solid = true
  Symmetric = false
